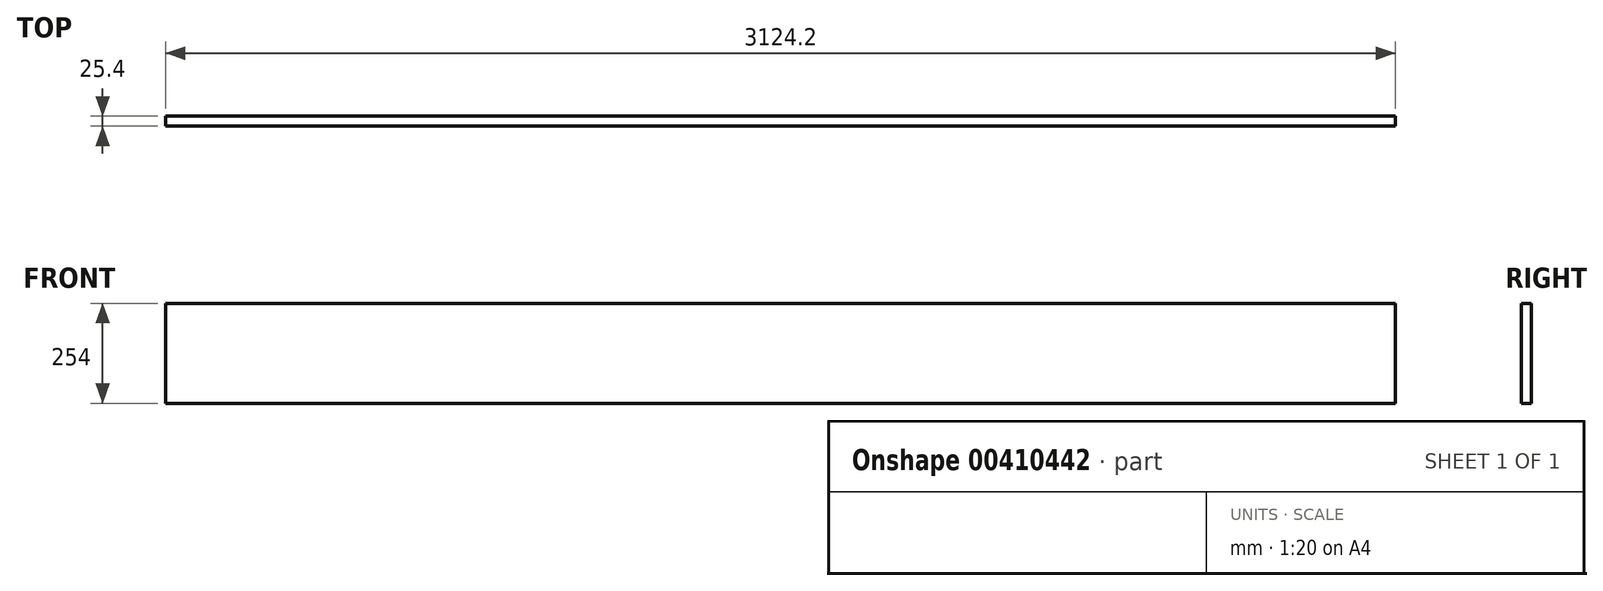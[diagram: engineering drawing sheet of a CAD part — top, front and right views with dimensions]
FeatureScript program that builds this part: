
annotation { "Feature Type Name" : "Feature", "Feature Type Description" : "" }
export const myFeature = defineFeature(function(context is Context, id is Id, definition is map)
    precondition{}
    {
        {
            var Q0;
            Q0=qCreatedBy(makeId("Front.planeOp"),FACE);
            var sketch = newSketch(context, id + "F0", { "sketchPlane" : qUnion([Q0])});
            skLineSegment(sketch, "E0.bottom", {"start": v(-1562.1, 127) * mm, "end": v(1562.1, 127) * mm});
            skLineSegment(sketch, "E0.top", {"start": v(-1562.1, -127) * mm, "end": v(1562.1, -127) * mm});
            skLineSegment(sketch, "E0.left", {"start": v(-1562.1, 127) * mm, "end": v(-1562.1, -127) * mm});
            skLineSegment(sketch, "E0.right", {"start": v(1562.1, 127) * mm, "end": v(1562.1, -127) * mm});
            skPoint(sketch, "E0.middle", {"position": v(0, 0) * mm});
            skSolve(sketch);
        }
        {
            var Q0;
            Q0=qSketchRegion(id+"F0",true);
            extrude(context, id + "F1", {"entities" : qUnion([Q0]), "depth" : 25.4 * mm, "offsetDistance" : 25.4 * mm});
        }
    });
